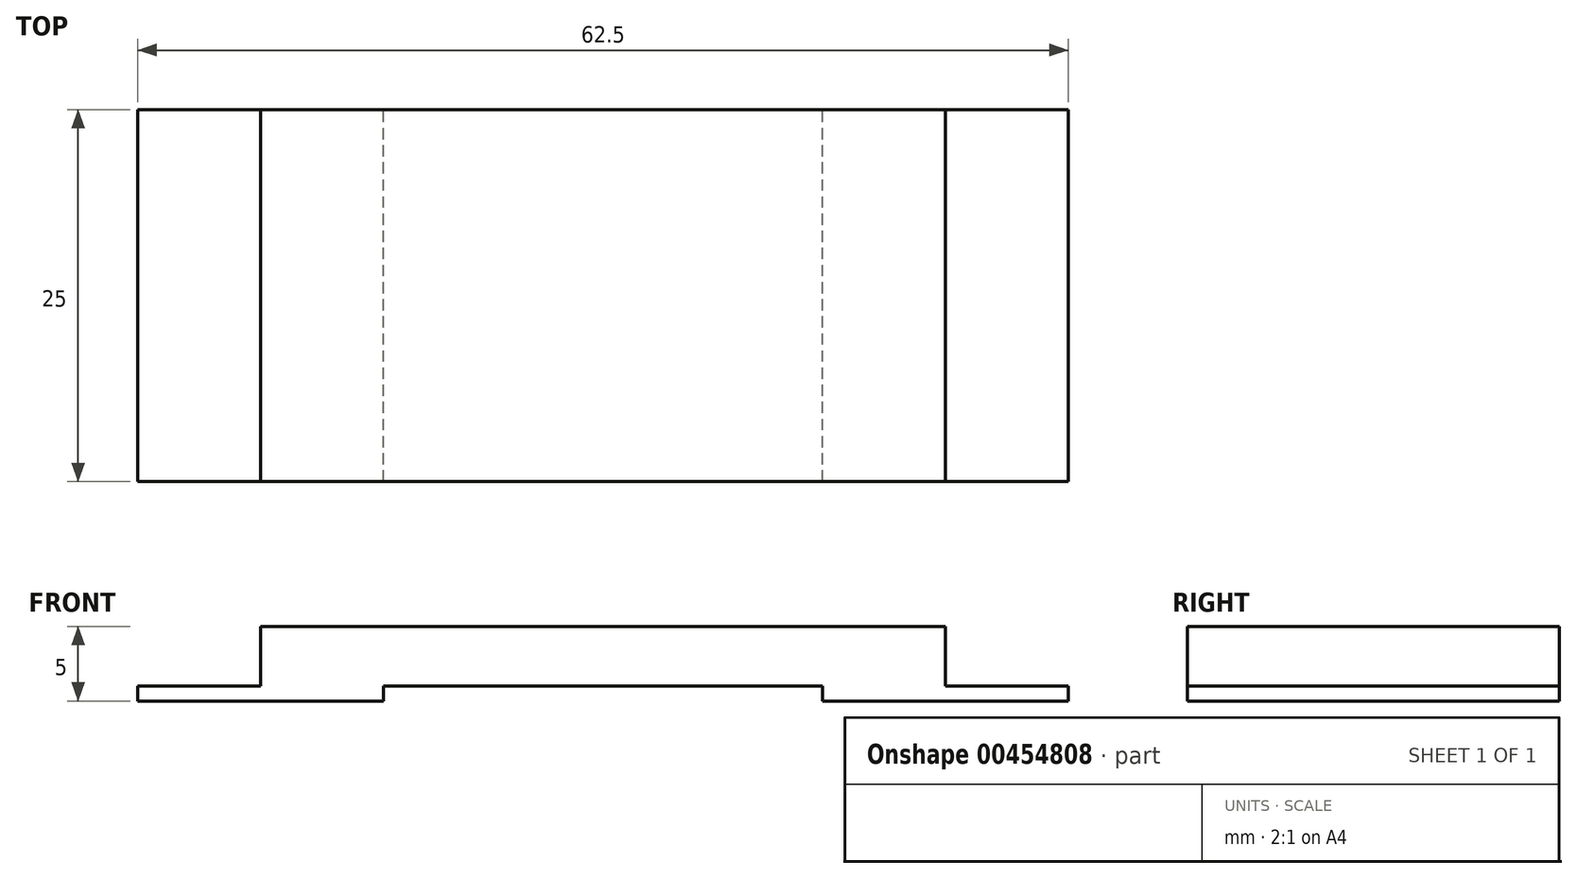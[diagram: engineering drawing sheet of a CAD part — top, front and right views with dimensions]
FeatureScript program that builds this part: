
annotation { "Feature Type Name" : "Feature", "Feature Type Description" : "" }
export const myFeature = defineFeature(function(context is Context, id is Id, definition is map)
    precondition{}
    {
        {
            var Q0;
            Q0=qCreatedBy(makeId("Front.planeOp"),FACE);
            var sketch = newSketch(context, id + "F0", { "sketchPlane" : qUnion([Q0])});
            skLineSegment(sketch, "E0", {"start": v(-26.36, -21.5) * mm, "end": v(19.64, -21.5) * mm});
            skLineSegment(sketch, "E1", {"start": v(19.64, -21.5) * mm, "end": v(19.64, -25.5) * mm});
            skLineSegment(sketch, "E2", {"start": v(19.64, -25.5) * mm, "end": v(27.89, -25.5) * mm});
            skLineSegment(sketch, "E3", {"start": v(27.89, -25.5) * mm, "end": v(27.89, -26.5) * mm});
            skLineSegment(sketch, "E4", {"start": v(27.89, -26.5) * mm, "end": v(11.39, -26.5) * mm});
            skLineSegment(sketch, "E5", {"start": v(11.39, -26.5) * mm, "end": v(11.39, -25.5) * mm});
            skLineSegment(sketch, "E6", {"start": v(11.39, -25.5) * mm, "end": v(-18.11, -25.5) * mm});
            skLineSegment(sketch, "E7", {"start": v(-18.11, -25.5) * mm, "end": v(-18.11, -26.5) * mm});
            skLineSegment(sketch, "E8", {"start": v(-18.11, -26.5) * mm, "end": v(-34.61, -26.5) * mm});
            skLineSegment(sketch, "E9", {"start": v(-34.61, -26.5) * mm, "end": v(-34.61, -25.5) * mm});
            skLineSegment(sketch, "E10", {"start": v(-34.61, -25.5) * mm, "end": v(-26.36, -25.5) * mm});
            skLineSegment(sketch, "E11", {"start": v(-26.36, -25.5) * mm, "end": v(-26.36, -21.5) * mm});
            skSolve(sketch);
        }
        {
            var Q0;
            Q0 = qSketchRegion(id + "F0", true);
            extrude(context, id + "F1", {"entities" : qUnion([Q0]), "depth" : 25 * mm});
        }
    });
